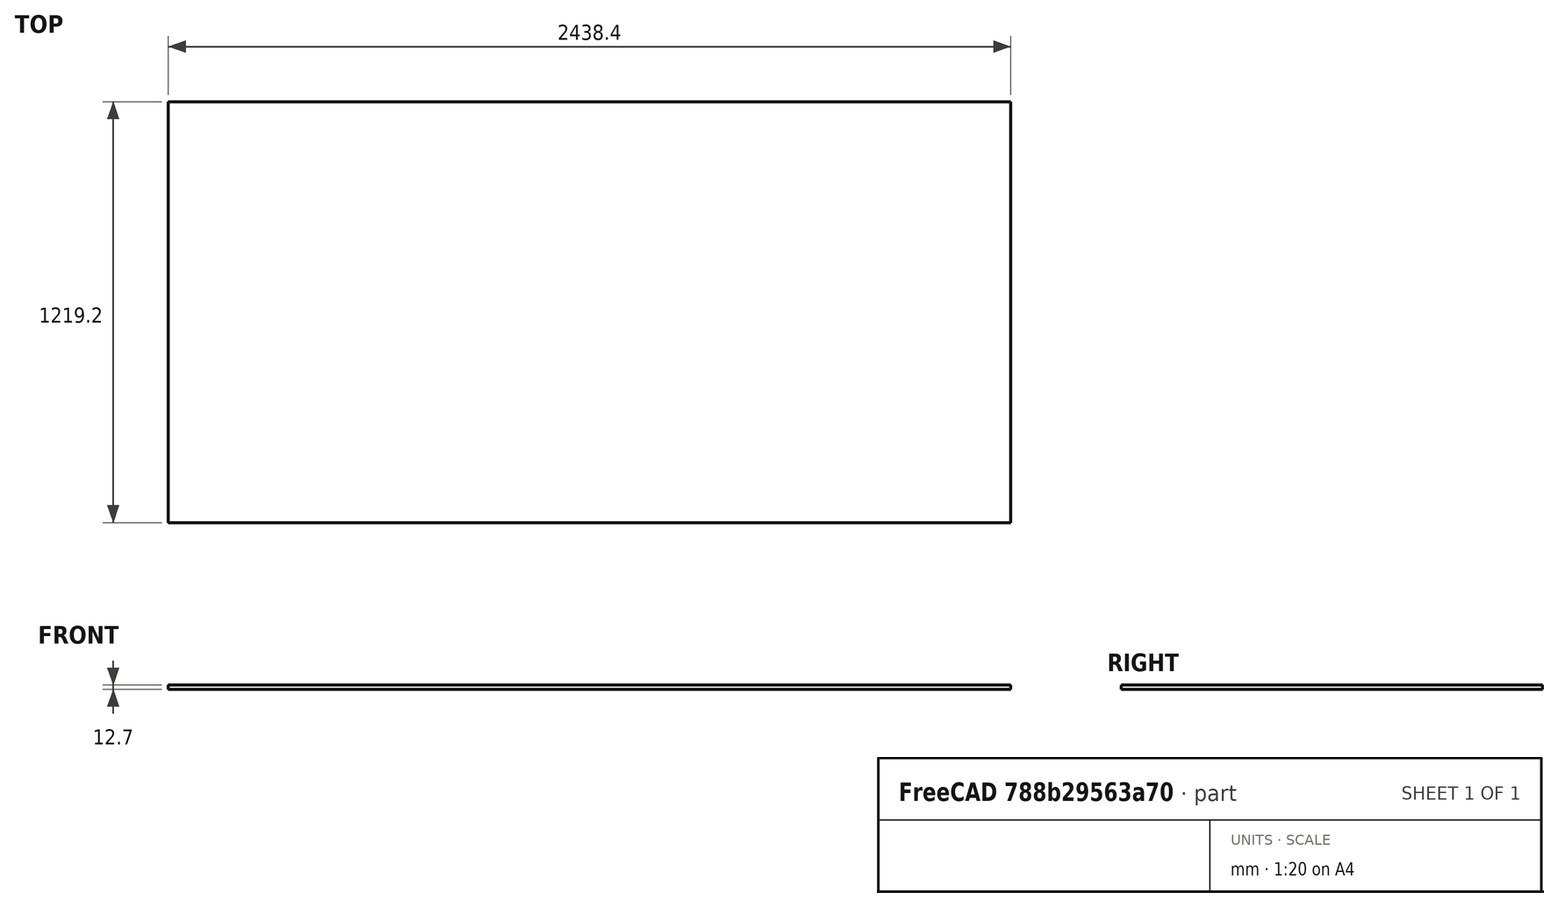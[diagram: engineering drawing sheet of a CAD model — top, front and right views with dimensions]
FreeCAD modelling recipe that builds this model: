
FCSTD DOCUMENT  (FreeCAD 0.19R24291 (Git))
Label: plywoodSheet4x8x0.5
License: All rights reserved
LicenseURL: http://en.wikipedia.org/wiki/All_rights_reserved
objects: Sketcher::SketchObject×1, PartDesign::Pad×1, PartDesign::Body×1
note: 4 computed .brp shape members not serialized (recipe doc carries the construction recipe); baked Part::Feature solids carry a one-line shape summary decoded from their .brp

FEATURE [Sketcher::SketchObject] Sketch
  FullyConstrained = true
  MapMode = 5
  Support = -> [XY_Plane]
  expr: Constraints[10] = 8 * 12 * 25.4
  expr: Constraints[9] = 4 * 12 * 25.4
  sketch-geometry (4):
    g0: LineSegment StartX=0 StartY=0 StartZ=0 EndX=2438.4 EndY=0 EndZ=0
    g1: LineSegment StartX=2438.4 StartY=0 StartZ=0 EndX=2438.4 EndY=1219.2 EndZ=0
    g2: LineSegment StartX=2438.4 StartY=1219.2 StartZ=0 EndX=0 EndY=1219.2 EndZ=0
    g3: LineSegment StartX=0 StartY=1219.2 StartZ=0 EndX=0 EndY=0 EndZ=0
  constraints (11):
    c: Coincident(g0,g1)
    c: Coincident(g1,g2)
    c: Coincident(g2,g3)
    c: Coincident(g3,g0)
    c: Horizontal(g0)
    c: Horizontal(g2)
    c: Vertical(g1)
    c: Vertical(g3)
    c: Coincident(g0,g-1)
    c: DistanceY(g3,g3) = 1219.2
    c: DistanceX(g0,g0) = 2438.4
FEATURE [PartDesign::Pad] Pad
  Direction = (1,1,1)
  Length = 12.7
  Length2 = 100
  Profile = -> Sketch
  Type = 0
  expr: Length = 0.5 * 25.4
FEATURE [PartDesign::Body] Body
  Group = -> [Sketch,Pad]
  Origin = -> Origin
  Tip = -> Pad
